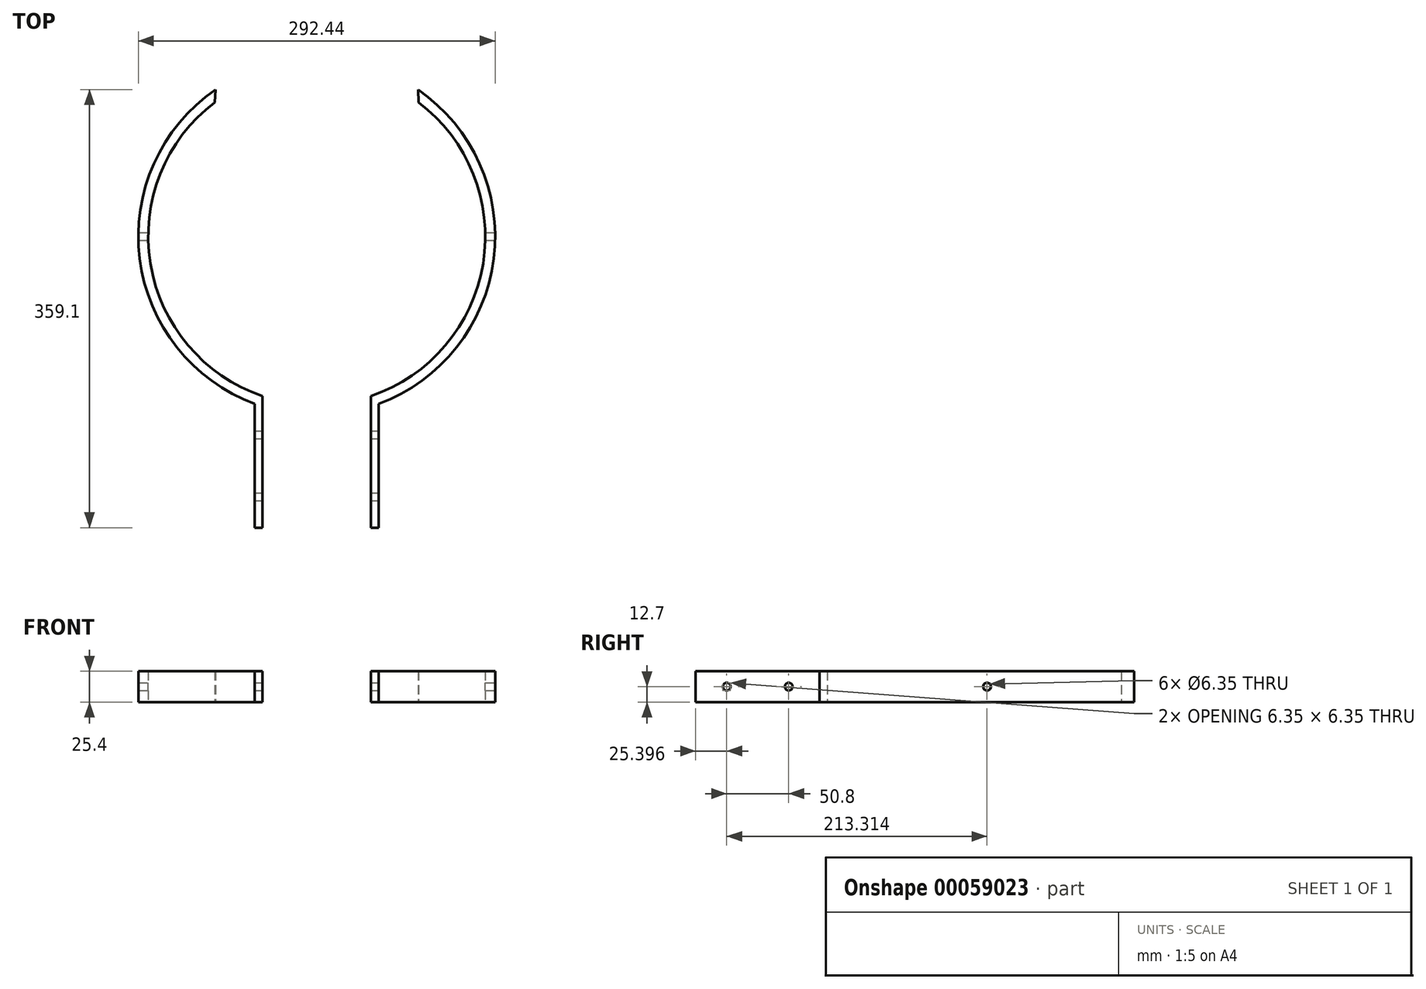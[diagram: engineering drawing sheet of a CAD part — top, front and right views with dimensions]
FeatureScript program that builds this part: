
annotation { "Feature Type Name" : "Feature", "Feature Type Description" : "" }
export const myFeature = defineFeature(function(context is Context, id is Id, definition is map)
    precondition{}
    {
        {
            var Q0;
            Q0=qCreatedBy(makeId("Top.planeOp"),FACE);
            var sketch = newSketch(context, id + "F0", { "sketchPlane" : qUnion([Q0])});
            skLineSegment(sketch, "E0", {"start": v(-44.45, -130.76) * mm, "end": v(-44.45, -238.71) * mm});
            skLineSegment(sketch, "E1", {"start": v(-44.45, -238.71) * mm, "end": v(-50.8, -238.71) * mm});
            skLineSegment(sketch, "E2", {"start": v(-50.8, -238.71) * mm, "end": v(-50.8, -137.11) * mm});
            skArc(sketch, "E3", {"start": v(-83.53, 110) * mm, "mid": v(-136.33, -22.13) * mm, "end": v(-44.45, -130.76) * mm});
            skArc(sketch, "E4", {"start": v(-82.98, 120.4) * mm, "mid": v(-145.1, -18.13) * mm, "end": v(-50.8, -137.11) * mm});
            skLineSegment(sketch, "E5", {"start": v(-82.98, 120.4) * mm, "end": v(-83.53, 110) * mm});
            skLineSegment(sketch, "E6.MirrorCS", {"start": v(82.98, 120.4) * mm, "end": v(83.53, 110) * mm});
            skLineSegment(sketch, "E7.MirrorCS", {"start": v(44.45, -238.71) * mm, "end": v(50.8, -238.71) * mm});
            skArc(sketch, "E8.MirrorCS", {"start": v(82.98, 120.4) * mm, "mid": v(145.1, -18.13) * mm, "end": v(50.8, -137.11) * mm});
            skLineSegment(sketch, "E9.MirrorCS", {"start": v(50.8, -238.71) * mm, "end": v(50.8, -137.11) * mm});
            skLineSegment(sketch, "E10.MirrorCS", {"start": v(44.45, -130.76) * mm, "end": v(44.45, -238.71) * mm});
            skArc(sketch, "E11.MirrorCS", {"start": v(83.53, 110) * mm, "mid": v(136.33, -22.13) * mm, "end": v(44.45, -130.76) * mm});
            skArc(sketch, "E12", {"start": v(137.78, -9.52) * mm, "mid": v(138.11, 0) * mm, "end": v(137.78, 9.53) * mm});
            skLineSegment(sketch, "E13", {"start": v(137.78, 9.53) * mm, "end": v(145.91, 9.53) * mm});
            skLineSegment(sketch, "E14", {"start": v(145.91, 9.53) * mm, "end": v(145.91, -9.52) * mm});
            skLineSegment(sketch, "E15", {"start": v(145.91, -9.52) * mm, "end": v(137.78, -9.52) * mm});
            skArc(sketch, "E16.MirrorCS", {"start": v(-137.78, -9.52) * mm, "mid": v(-138.11, 0) * mm, "end": v(-137.78, 9.53) * mm});
            skLineSegment(sketch, "E17.MirrorCS", {"start": v(-145.91, -9.52) * mm, "end": v(-137.78, -9.52) * mm});
            skLineSegment(sketch, "E18.MirrorCS", {"start": v(-137.78, 9.53) * mm, "end": v(-145.91, 9.53) * mm});
            skLineSegment(sketch, "E19.MirrorCS", {"start": v(-145.91, 9.53) * mm, "end": v(-145.91, -9.52) * mm});
            skSolve(sketch);
        }
        {
            var Q0;
            Q0=qSketchRegion(id+"F0",true);
            extrude(context, id + "F1", {"entities" : qUnion([Q0]), "depth" : 25.4 * mm});
        }
        {
            var Q0;
            Q0=qCreatedBy(makeId("Right.planeOp"),FACE);
            var sketch = newSketch(context, id + "F2", { "sketchPlane" : qUnion([Q0])});
            skCircle(sketch, "E20", {"center": v(0, 12.7) * mm, "radius": 3.18 * mm});
            skCircle(sketch, "E21", {"center": v(-162.51, 12.7) * mm, "radius": 3.18 * mm});
            skCircle(sketch, "E22", {"center": v(-213.31, 12.7) * mm, "radius": 3.18 * mm});
            skSolve(sketch);
        }
        {
            var Q0;
            Q0=qSketchRegion(id+"F2",true);
            extrude(context, id + "F3", {"entities" : qUnion([Q0]), "operationType" : NewBodyOperationType.REMOVE, "endBound" : BoundingType.SYMMETRIC, "oppositeDirection" : true, "depth" : 406.4 * mm});
        }
    });
